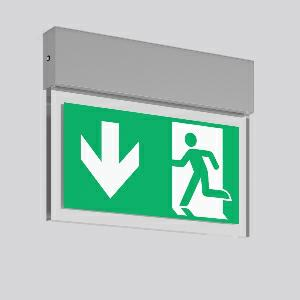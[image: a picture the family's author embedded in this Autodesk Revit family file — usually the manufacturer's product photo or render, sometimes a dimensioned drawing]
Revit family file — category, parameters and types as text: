
# Revit family: halyxx_671913_004_1_a611
name_source: partatom
category: Lighting Fixtures
units: mm (PartAtom-declared; Revit-internal decimal feet)

## family parameters
Cut with Voids When Loaded = No
Host = Face
Light Source = No
Part Type = Normal
Room Calculation Point = No
Round Connector Dimension = Use Diameter
Shared = No

## types (1)
- HALYXX (1 x LED Modul 840, 95 lm, 4000)
    Apparent Load = 4 VA
    Approval mark = CE
    CIE Flux Codes = 18 45 74 52 100
    Color Rendering = 80
    Color Temperature = 4000
    Default Elevation = 1800 mm
    Description = Series: HALYXX
Luminaire for escape route identification. Housing: extruded aluminium profile, anodised or powder-coated. Display panel: highly transparent panel, plastic, with legend on one side/both sides. Electronic ballast included. Self-contained system with automatic self-test. Please indicate legend number when placing your order! 
Colour: anodised aluminium
Length: 340 mm
Width: 40 mm
Height: 270 mm
Weight: 2.18 kg
Operating mode: maintained power mode
Viewing Distance: 30 m
Duration time: 8 h
Lamp: LED
Socket: without socket
Colour temperature: 4000K
Colour rendering index (CRI): 80
System power: 4.2 W
Rated luminous flux: 95 lm
Luminous flux, emergency: 6
System power, emergency: -
Control gear: Electronic transformer
Protection class: I
Type of protection: IP 40
    Height = 270 mm
    Lamp = 1 x LED Modul 840
    Lamp Light Flux = 95 lm
    Lamp count = 1
    Length = 340 mm
    Lifetime = 50000 h
    Luminous efficacy = 23 lm/W
    Manufacturer = RZB
    ModVariant = No
    Model = 671913.004.1
    Mounting Place = Ceiling
    Mounting Type = Surface mounted
    Number of Poles = 1
    OnlyDefault = Yes
    Power Factor = 1
    Product Name = HALYXX
    Product group = Surface mounted ceiling luminaires
    ProductGroupID = 303
    Protection Class = Protection class I
    Protection Degree = IP 40
    RLX_Detail_Level = 1
    RLX_Emergency_Light_Flux = 6 lm
    RLX_Emergency_Type = 3
    RLX_Emergency_Type_DB = Yes
    RlxData = <blob elided: 54821 chars, md5=90e796bd>
    Socket = socket
    Standby Power = 0 W
    System Light Flux = 95 lm
    System Power = 4 W
    Type Comments = Product without accessories
    Type Image = 671744.004.jpg
    URL = http://relux.com
    VarID = ---
    Voltage = 230 V
    Voltage Range = 220-240 V
    Weight = 0.00 kg
    Width = 40 mm  [stored 0.131234 ft]

note: [stored X ft] marks values corroborated as IEEE doubles in the binary element streams (Revit-internal decimal feet)

## geometry (parser evidence)
native form markers: Blend x4, Sweep x15
no freeform markers — native parametric forms only
